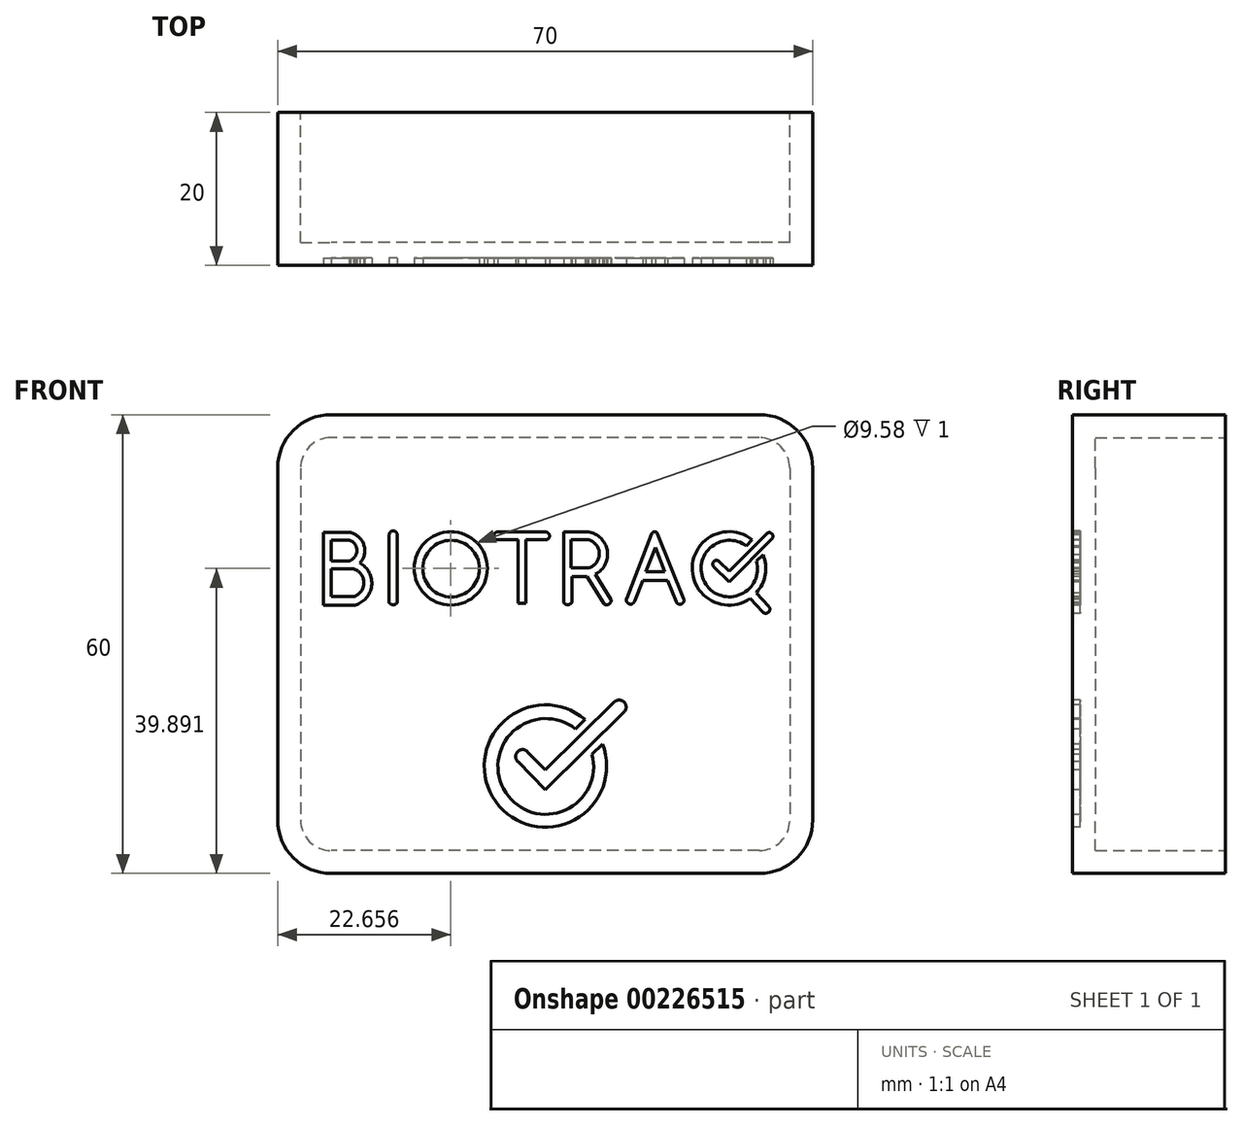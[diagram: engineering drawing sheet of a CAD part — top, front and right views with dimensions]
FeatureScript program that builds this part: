
annotation { "Feature Type Name" : "Feature", "Feature Type Description" : "" }
export const myFeature = defineFeature(function(context is Context, id is Id, definition is map)
    precondition{}
    {
        {
            var Q0;
            Q0=qCreatedBy(makeId("Front.planeOp"),FACE);
            var sketch = newSketch(context, id + "F0", { "sketchPlane" : qUnion([Q0])});
            skLineSegment(sketch, "E0.bottom", {"start": v(35, 30) * mm, "end": v(-35, 30) * mm});
            skLineSegment(sketch, "E0.top", {"start": v(35, -30) * mm, "end": v(-35, -30) * mm});
            skLineSegment(sketch, "E0.left", {"start": v(35, 30) * mm, "end": v(35, -30) * mm});
            skLineSegment(sketch, "E0.right", {"start": v(-35, 30) * mm, "end": v(-35, -30) * mm});
            skPoint(sketch, "E0.middle", {"position": v(0, 0) * mm});
            skSolve(sketch);
        }
        {
            var Q0;
            Q0 = qSketchRegion(id + "F0", true);
            extrude(context, id + "F1", {"entities" : qUnion([Q0]), "depth" : 20 * mm});
        }
        {
            var Q0;
            Q0=makeQuery(id+"F1.opExtrude","SWEPT_EDGE",EDGE,{"disambiguationData":[OSD([sQuery(id+"F0.wireOp",EDGE,"E0.top"),sQuery(id+"F0.wireOp",EDGE,"E0.left")])]});
            var Q1;
            Q1=makeQuery(id+"F1.opExtrude","SWEPT_EDGE",EDGE,{"disambiguationData":[OSD([sQuery(id+"F0.wireOp",EDGE,"E0.top"),sQuery(id+"F0.wireOp",EDGE,"E0.right")])]});
            var Q2;
            Q2=makeQuery(id+"F1.opExtrude","SWEPT_EDGE",EDGE,{"disambiguationData":[OSD([sQuery(id+"F0.wireOp",EDGE,"E0.bottom"),sQuery(id+"F0.wireOp",EDGE,"E0.left")])]});
            var Q3;
            Q3=makeQuery(id+"F1.opExtrude","SWEPT_EDGE",EDGE,{"disambiguationData":[OSD([sQuery(id+"F0.wireOp",EDGE,"E0.bottom"),sQuery(id+"F0.wireOp",EDGE,"E0.right")])]});
            fillet(context, id + "F2", {"entities" : qUnion([Q0, Q1, Q2, Q3]), "radius" : 7 * mm, "tangentPropagation" : true, "allowEdgeOverflow" : false});
        }
        {
            var Q0;
            Q0=makeQuery(id+"F1.opExtrude","CAP_FACE",FACE,{"disambiguationData":[OSD([sQuery(id+"F0.wireOp",EDGE,"E0.bottom"),sQuery(id+"F0.wireOp",EDGE,"E0.top"),sQuery(id+"F0.wireOp",EDGE,"E0.left"),sQuery(id+"F0.wireOp",EDGE,"E0.right")])],"isStart":true});
            shell(context, id + "F3", {"entities" : qUnion([Q0]), "thickness" : 3 * mm});
        }
        {
            var Q0;
            Q0=makeQuery(id+"F1.opExtrude","CAP_FACE",FACE,{"disambiguationData":[OSD([sQuery(id+"F0.wireOp",EDGE,"E0.bottom"),sQuery(id+"F0.wireOp",EDGE,"E0.top"),sQuery(id+"F0.wireOp",EDGE,"E0.left"),sQuery(id+"F0.wireOp",EDGE,"E0.right")])],"isStart":false});
            var sketch = newSketch(context, id + "F4", { "sketchPlane" : qUnion([Q0])});
            skCircle(sketch, "E1", {"center": v(0.04, -15.96) * mm, "radius": 8 * mm});
            skPoint(sketch, "E1.first.point", {"position": v(-2.89, -8.5) * mm});
            skPoint(sketch, "E1.second.point", {"position": v(-1.08, -23.88) * mm});
            skPoint(sketch, "E1.third.point", {"position": v(8.03, -16.41) * mm});
            skCircle(sketch, "E2", {"center": v(0.08, -16) * mm, "radius": 6.26 * mm});
            skPoint(sketch, "E2.first.point", {"position": v(-2.06, -10.12) * mm});
            skPoint(sketch, "E2.second.point", {"position": v(5.93, -18.23) * mm});
            skPoint(sketch, "E2.third.point", {"position": v(-2.53, -21.7) * mm});
            skLineSegment(sketch, "E3", {"start": v(0.04, -16.45) * mm, "end": v(9.02, -7.59) * mm});
            skLineSegment(sketch, "E4", {"start": v(0.04, -16.45) * mm, "end": v(-2.3, -14.07) * mm});
            skLineSegment(sketch, "E5", {"start": v(-3.56, -15.39) * mm, "end": v(0.04, -19.04) * mm});
            skLineSegment(sketch, "E6", {"start": v(0.04, -19.04) * mm, "end": v(10.32, -8.9) * mm});
            skArc(sketch, "E7", {"start": v(10.32, -8.9) * mm, "mid": v(10.32, -7.6) * mm, "end": v(9.02, -7.59) * mm});
            skLineSegment(sketch, "E8", {"start": v(5.2, -9.84) * mm, "end": v(3.95, -11.09) * mm});
            skLineSegment(sketch, "E9", {"start": v(7.5, -13.07) * mm, "end": v(6.13, -14.42) * mm});
            skLineSegment(sketch, "E10", {"start": v(-29.01, 14.58) * mm, "end": v(-29.01, 5.08) * mm});
            skLineSegment(sketch, "E11", {"start": v(-29.01, 5.08) * mm, "end": v(-24.9, 5.08) * mm});
            skLineSegment(sketch, "E12", {"start": v(-29.01, 14.58) * mm, "end": v(-25.46, 14.58) * mm});
            skLineSegment(sketch, "E13", {"start": v(-27.97, 13.59) * mm, "end": v(-27.97, 10.87) * mm});
            skLineSegment(sketch, "E14", {"start": v(-27.97, 10.87) * mm, "end": v(-25.64, 10.87) * mm});
            skLineSegment(sketch, "E15", {"start": v(-27.97, 13.59) * mm, "end": v(-25.62, 13.59) * mm});
            skLineSegment(sketch, "E16", {"start": v(-25.08, 9.84) * mm, "end": v(-27.96, 9.84) * mm});
            skLineSegment(sketch, "E17", {"start": v(-27.96, 9.84) * mm, "end": v(-27.96, 6.19) * mm});
            skArc(sketch, "E18", {"start": v(-24.23, 10.58) * mm, "mid": v(-23.7, 12.93) * mm, "end": v(-25.46, 14.58) * mm});
            skArc(sketch, "E19", {"start": v(-25.64, 10.87) * mm, "mid": v(-24.62, 12.22) * mm, "end": v(-25.62, 13.59) * mm});
            skArc(sketch, "E20", {"start": v(-24.9, 5.08) * mm, "mid": v(-22.7, 7.6) * mm, "end": v(-24.23, 10.58) * mm});
            skArc(sketch, "E21", {"start": v(-25.08, 6.2) * mm, "mid": v(-23.71, 8.02) * mm, "end": v(-25.08, 9.84) * mm});
            skLineSegment(sketch, "E22", {"start": v(-27.96, 6.19) * mm, "end": v(-25.08, 6.2) * mm});
            skLineSegment(sketch, "E23", {"start": v(-20.4, 14.3) * mm, "end": v(-20.4, 5.4) * mm});
            skLineSegment(sketch, "E24", {"start": v(-19.37, 14.29) * mm, "end": v(-19.37, 5.4) * mm});
            skArc(sketch, "E25", {"start": v(-19.37, 14.29) * mm, "mid": v(-19.88, 14.8) * mm, "end": v(-20.4, 14.3) * mm});
            skArc(sketch, "E26", {"start": v(-20.4, 5.4) * mm, "mid": v(-19.88, 5.13) * mm, "end": v(-19.37, 5.4) * mm});
            skCircle(sketch, "E27", {"center": v(-12.34, 9.9) * mm, "radius": 4.79 * mm});
            skPoint(sketch, "E27.first.point", {"position": v(-14.18, 14.31) * mm});
            skPoint(sketch, "E27.second.point", {"position": v(-7.82, 8.33) * mm});
            skPoint(sketch, "E27.third.point", {"position": v(-14.48, 5.6) * mm});
            skCircle(sketch, "E28", {"center": v(-12.3, 9.86) * mm, "radius": 3.7 * mm});
            skPoint(sketch, "E28.first.point", {"position": v(-13.14, 13.47) * mm});
            skPoint(sketch, "E28.second.point", {"position": v(-9.02, 8.16) * mm});
            skPoint(sketch, "E28.third.point", {"position": v(-13.27, 6.29) * mm});
            skLineSegment(sketch, "E29", {"start": v(-6.23, 14.65) * mm, "end": v(0.06, 14.65) * mm});
            skLineSegment(sketch, "E30", {"start": v(0.06, 14.65) * mm, "end": v(0.06, 13.63) * mm});
            skLineSegment(sketch, "E31", {"start": v(0.06, 13.63) * mm, "end": v(-2.55, 13.63) * mm});
            skLineSegment(sketch, "E32", {"start": v(-2.55, 13.63) * mm, "end": v(-2.55, 5.34) * mm});
            skLineSegment(sketch, "E33", {"start": v(-2.55, 5.34) * mm, "end": v(-3.57, 5.34) * mm});
            skLineSegment(sketch, "E34", {"start": v(-3.57, 5.34) * mm, "end": v(-3.57, 13.63) * mm});
            skLineSegment(sketch, "E35", {"start": v(-3.57, 13.63) * mm, "end": v(-6.23, 13.63) * mm});
            skLineSegment(sketch, "E36", {"start": v(-6.23, 13.63) * mm, "end": v(-6.23, 14.65) * mm});
            skArc(sketch, "E37", {"start": v(-6.23, 14.65) * mm, "mid": v(-6.74, 14.14) * mm, "end": v(-6.23, 13.63) * mm});
            skArc(sketch, "E38", {"start": v(0.06, 13.63) * mm, "mid": v(0.57, 14.14) * mm, "end": v(0.06, 14.65) * mm});
            skArc(sketch, "E39", {"start": v(-3.57, 5.34) * mm, "mid": v(-3.06, 5.06) * mm, "end": v(-2.55, 5.34) * mm});
            skLineSegment(sketch, "E40", {"start": v(2.4, 14.65) * mm, "end": v(2.4, 5.45) * mm});
            skLineSegment(sketch, "E41", {"start": v(3.5, 5.45) * mm, "end": v(3.5, 8.84) * mm});
            skLineSegment(sketch, "E42", {"start": v(3.5, 8.84) * mm, "end": v(5.47, 8.84) * mm});
            skLineSegment(sketch, "E43", {"start": v(5.47, 8.84) * mm, "end": v(7.66, 5.26) * mm});
            skLineSegment(sketch, "E44", {"start": v(8.61, 5.84) * mm, "end": v(6.58, 9.15) * mm});
            skLineSegment(sketch, "E45", {"start": v(5.6, 9.94) * mm, "end": v(3.37, 9.94) * mm});
            skLineSegment(sketch, "E46", {"start": v(3.37, 9.94) * mm, "end": v(3.37, 13.63) * mm});
            skLineSegment(sketch, "E47", {"start": v(3.37, 13.63) * mm, "end": v(5.69, 13.63) * mm});
            skLineSegment(sketch, "E48", {"start": v(5.69, 14.65) * mm, "end": v(2.4, 14.65) * mm});
            skArc(sketch, "E49", {"start": v(6.58, 9.15) * mm, "mid": v(8.13, 12.22) * mm, "end": v(5.69, 14.65) * mm});
            skArc(sketch, "E50", {"start": v(5.6, 9.94) * mm, "mid": v(7.08, 11.75) * mm, "end": v(5.69, 13.63) * mm});
            skArc(sketch, "E51", {"start": v(7.66, 5.26) * mm, "mid": v(8.35, 5.21) * mm, "end": v(8.61, 5.84) * mm});
            skArc(sketch, "E52", {"start": v(2.4, 5.45) * mm, "mid": v(2.95, 5.14) * mm, "end": v(3.5, 5.45) * mm});
            skLineSegment(sketch, "E53", {"start": v(13.93, 14.4) * mm, "end": v(10.65, 5.98) * mm});
            skLineSegment(sketch, "E54", {"start": v(11.7, 5.58) * mm, "end": v(12.77, 8.33) * mm});
            skLineSegment(sketch, "E55", {"start": v(12.77, 8.33) * mm, "end": v(16, 8.33) * mm});
            skLineSegment(sketch, "E56", {"start": v(16, 8.33) * mm, "end": v(17.13, 5.53) * mm});
            skLineSegment(sketch, "E57", {"start": v(18.11, 5.92) * mm, "end": v(14.7, 14.42) * mm});
            skLineSegment(sketch, "E58", {"start": v(14.41, 12.65) * mm, "end": v(15.64, 9.48) * mm});
            skLineSegment(sketch, "E59", {"start": v(15.64, 9.48) * mm, "end": v(13.14, 9.48) * mm});
            skLineSegment(sketch, "E60", {"start": v(13.14, 9.48) * mm, "end": v(14.41, 12.65) * mm});
            skArc(sketch, "E61", {"start": v(14.7, 14.42) * mm, "mid": v(14.31, 14.68) * mm, "end": v(13.93, 14.4) * mm});
            skArc(sketch, "E62", {"start": v(17.13, 5.53) * mm, "mid": v(17.82, 5.23) * mm, "end": v(18.11, 5.92) * mm});
            skArc(sketch, "E63", {"start": v(10.65, 5.98) * mm, "mid": v(10.97, 5.26) * mm, "end": v(11.7, 5.58) * mm});
            skCircle(sketch, "E64", {"center": v(24.1, 9.87) * mm, "radius": 3.7 * mm});
            skPoint(sketch, "E64.first.point", {"position": v(22.89, 13.37) * mm});
            skPoint(sketch, "E64.second.point", {"position": v(27.78, 9.76) * mm});
            skPoint(sketch, "E64.third.point", {"position": v(22.44, 6.57) * mm});
            skCircle(sketch, "E65", {"center": v(24.05, 9.9) * mm, "radius": 4.8 * mm});
            skPoint(sketch, "E65.first.point", {"position": v(21.54, 14) * mm});
            skPoint(sketch, "E65.second.point", {"position": v(28.67, 8.6) * mm});
            skPoint(sketch, "E65.third.point", {"position": v(22.44, 5.36) * mm});
            skLineSegment(sketch, "E66", {"start": v(24.07, 8.1) * mm, "end": v(29.65, 13.75) * mm});
            skLineSegment(sketch, "E67", {"start": v(28.95, 14.43) * mm, "end": v(24.1, 9.5) * mm});
            skLineSegment(sketch, "E68", {"start": v(24.1, 9.5) * mm, "end": v(22.78, 10.8) * mm});
            skLineSegment(sketch, "E69", {"start": v(22.06, 10.1) * mm, "end": v(24.07, 8.1) * mm});
            skArc(sketch, "E70", {"start": v(22.78, 10.8) * mm, "mid": v(22.06, 10.8) * mm, "end": v(22.06, 10.1) * mm});
            skArc(sketch, "E71", {"start": v(29.65, 13.75) * mm, "mid": v(29.64, 14.44) * mm, "end": v(28.95, 14.43) * mm});
            skLineSegment(sketch, "E72", {"start": v(27.06, 13.63) * mm, "end": v(26.33, 12.81) * mm});
            skLineSegment(sketch, "E73", {"start": v(27.66, 10.84) * mm, "end": v(28.5, 11.7) * mm});
            skArc(sketch, "E74", {"start": v(-2.3, -14.07) * mm, "mid": v(-3.62, -14.08) * mm, "end": v(-3.56, -15.39) * mm});
            skLineSegment(sketch, "E75", {"start": v(4.65, -22.5) * mm, "end": v(7.7, -25.82) * mm});
            skLineSegment(sketch, "E76", {"start": v(9, -24.62) * mm, "end": v(5.98, -21.32) * mm});
            skArc(sketch, "E77", {"start": v(7.7, -25.82) * mm, "mid": v(8.94, -25.87) * mm, "end": v(9, -24.62) * mm});
            skLineSegment(sketch, "E78", {"start": v(27.63, 6.7) * mm, "end": v(29.25, 4.93) * mm});
            skLineSegment(sketch, "E79", {"start": v(28.44, 4.2) * mm, "end": v(26.82, 5.96) * mm});
            skArc(sketch, "E80", {"start": v(28.44, 4.2) * mm, "mid": v(29.21, 4.16) * mm, "end": v(29.25, 4.93) * mm});
            skSolve(sketch);
        }
        {
            var Q0;
            {var subQ4=sQuery(id+"F4.wireOp",EDGE,"E8");Q0=makeQuery(id+"F4.imprint","IMPRINT",FACE,{"disambiguationData":[TD([[makeQuery(id+"F4.imprint","IMPRINT",EDGE,{"derivedFrom":subQ4}),-1.0]])]});}
            var Q1;
            {var subQ1=sQuery(id+"F4.wireOp",EDGE,"E4");Q1=makeQuery(id+"F4.imprint","IMPRINT",FACE,{"disambiguationData":[TD([[makeQuery(id+"F4.imprint","IMPRINT",EDGE,{"derivedFrom":subQ1}),1.0]])]});}
            var Q2;
            {var subQ0=sQuery(id+"F4.wireOp",EDGE,"E6");var subQ1=sQuery(id+"F4.wireOp",EDGE,"E1");var subQ2=makeQuery(id+"F4.imprint","INTERSECT",VERTEX,{"derivedFrom":[subQ1,subQ0]});Q2=makeQuery(id+"F4.imprint","IMPRINT",FACE,{"disambiguationData":[TD([[makeQuery(id+"F4.imprint","IMPRINT",EDGE,{"disambiguationData":[TD([[subQ2,-1.0]])],"derivedFrom":subQ1}),1.0]])]});}
            var Q3;
            {var subQ5=sQuery(id+"F4.wireOp",EDGE,"E7");Q3=makeQuery(id+"F4.imprint","IMPRINT",FACE,{"disambiguationData":[TD([[makeQuery(id+"F4.imprint","IMPRINT",EDGE,{"derivedFrom":subQ5}),1.0]])]});}
            var Q4;
            Q4=makeQuery(id+"F4.imprint","IMPRINT",FACE,{"disambiguationData":[TD([[makeQuery(id+"F4.imprint","IMPRINT",EDGE,{"derivedFrom":sQuery(id+"F4.wireOp",EDGE,"E10")}),1.0]])]});
            var Q5;
            Q5=makeQuery(id+"F4.imprint","IMPRINT",FACE,{"disambiguationData":[TD([[makeQuery(id+"F4.imprint","IMPRINT",EDGE,{"derivedFrom":sQuery(id+"F4.wireOp",EDGE,"E23")}),1.0]])]});
            var Q6;
            Q6=makeQuery(id+"F4.imprint","IMPRINT",FACE,{"disambiguationData":[TD([[makeQuery(id+"F4.imprint","IMPRINT",EDGE,{"derivedFrom":sQuery(id+"F4.wireOp",EDGE,"E27")}),1.0]])]});
            var Q7;
            Q7=makeQuery(id+"F4.imprint","IMPRINT",FACE,{"disambiguationData":[TD([[makeQuery(id+"F4.imprint","IMPRINT",EDGE,{"derivedFrom":sQuery(id+"F4.wireOp",EDGE,"E29")}),-1.0]])]});
            var Q8;
            Q8=makeQuery(id+"F4.imprint","IMPRINT",FACE,{"disambiguationData":[TD([[makeQuery(id+"F4.imprint","IMPRINT",EDGE,{"derivedFrom":sQuery(id+"F4.wireOp",EDGE,"E30")}),1.0]])]});
            var Q9;
            Q9=makeQuery(id+"F4.imprint","IMPRINT",FACE,{"disambiguationData":[TD([[makeQuery(id+"F4.imprint","IMPRINT",EDGE,{"derivedFrom":sQuery(id+"F4.wireOp",EDGE,"E36")}),1.0]])]});
            var Q10;
            Q10=makeQuery(id+"F4.imprint","IMPRINT",FACE,{"disambiguationData":[TD([[makeQuery(id+"F4.imprint","IMPRINT",EDGE,{"derivedFrom":sQuery(id+"F4.wireOp",EDGE,"E40")}),1.0]])]});
            var Q11;
            Q11=makeQuery(id+"F4.imprint","IMPRINT",FACE,{"disambiguationData":[TD([[makeQuery(id+"F4.imprint","IMPRINT",EDGE,{"derivedFrom":sQuery(id+"F4.wireOp",EDGE,"E53")}),1.0]])]});
            var Q12;
            {var subQ4=sQuery(id+"F4.wireOp",EDGE,"E72");Q12=makeQuery(id+"F4.imprint","IMPRINT",FACE,{"disambiguationData":[TD([[makeQuery(id+"F4.imprint","IMPRINT",EDGE,{"derivedFrom":subQ4}),-1.0]])]});}
            var Q13;
            {var subQ0=sQuery(id+"F4.wireOp",EDGE,"E68");Q13=makeQuery(id+"F4.imprint","IMPRINT",FACE,{"disambiguationData":[TD([[makeQuery(id+"F4.imprint","IMPRINT",EDGE,{"derivedFrom":subQ0}),1.0]])]});}
            var Q14;
            {var subQ0=sQuery(id+"F4.wireOp",EDGE,"E78");Q14=makeQuery(id+"F4.imprint","IMPRINT",FACE,{"disambiguationData":[TD([[makeQuery(id+"F4.imprint","IMPRINT",EDGE,{"derivedFrom":subQ0}),-1.0]])]});}
            var Q15;
            {var subQ5=sQuery(id+"F4.wireOp",EDGE,"E71");Q15=makeQuery(id+"F4.imprint","IMPRINT",FACE,{"disambiguationData":[TD([[makeQuery(id+"F4.imprint","IMPRINT",EDGE,{"derivedFrom":subQ5}),1.0]])]});}
            var Q16;
            {var subQ0=sQuery(id+"F4.wireOp",EDGE,"E66");var subQ1=sQuery(id+"F4.wireOp",EDGE,"E64");var subQ2=makeQuery(id+"F4.imprint","INTERSECT",VERTEX,{"derivedFrom":[subQ1,subQ0]});Q16=makeQuery(id+"F4.imprint","IMPRINT",FACE,{"disambiguationData":[TD([[makeQuery(id+"F4.imprint","IMPRINT",EDGE,{"disambiguationData":[TD([[subQ2,-1.0]])],"derivedFrom":subQ1}),-1.0]])]});}
            extrude(context, id + "F5", {"entities" : qUnion([Q0, Q1, Q2, Q3, Q4, Q5, Q6, Q7, Q8, Q9, Q10, Q11, Q12, Q13, Q14, Q15, Q16]), "operationType" : NewBodyOperationType.REMOVE, "oppositeDirection" : true, "depth" : 1 * mm});
        }
    });
